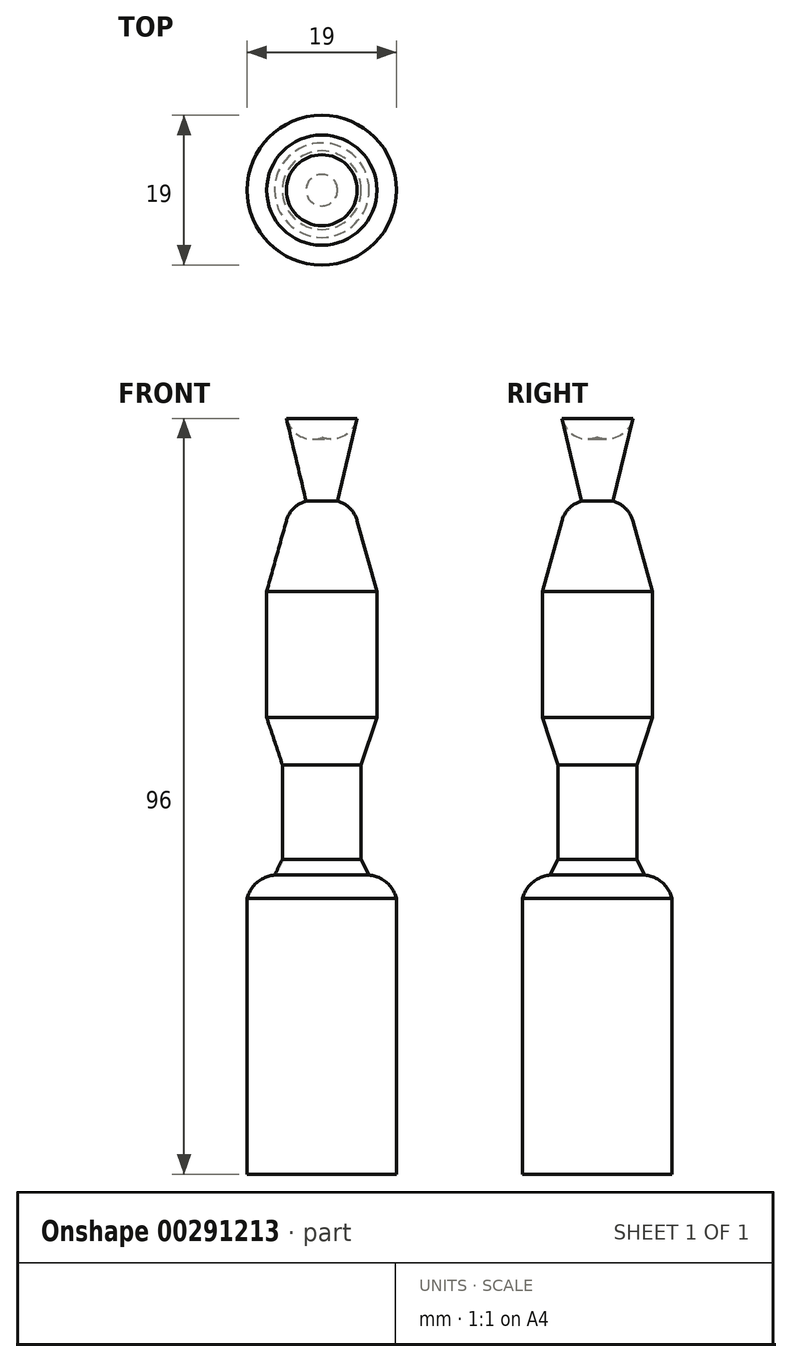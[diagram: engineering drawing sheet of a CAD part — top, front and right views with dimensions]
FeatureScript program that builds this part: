
annotation { "Feature Type Name" : "Feature", "Feature Type Description" : "" }
export const myFeature = defineFeature(function(context is Context, id is Id, definition is map)
    precondition{}
    {
        {
            var Q0;
            Q0=qCreatedBy(makeId("Front.planeOp"),FACE);
            var sketch = newSketch(context, id + "F0", { "sketchPlane" : qUnion([Q0])});
            skLineSegment(sketch, "E0", {"start": v(4.5, -4) * mm, "end": v(2, -14.5) * mm});
            skArc(sketch, "E1", {"start": v(4.5, -17) * mm, "mid": v(3.58, -15.42) * mm, "end": v(2, -14.5) * mm});
            skLineSegment(sketch, "E2", {"start": v(4.5, -17) * mm, "end": v(7, -26) * mm});
            skLineSegment(sketch, "E3", {"start": v(7, -26) * mm, "end": v(7, -42) * mm});
            skLineSegment(sketch, "E4", {"start": v(7, -42) * mm, "end": v(5, -48) * mm});
            skLineSegment(sketch, "E5", {"start": v(5, -48) * mm, "end": v(5, -60) * mm});
            skArc(sketch, "E6", {"start": v(9.5, -65) * mm, "mid": v(8.23, -62.95) * mm, "end": v(6, -62) * mm});
            skLineSegment(sketch, "E7", {"start": v(9.5, -65) * mm, "end": v(9.5, -100) * mm});
            skLineSegment(sketch, "E8", {"start": v(9.5, -100) * mm, "end": v(0, -100) * mm});
            skLineSegment(sketch, "E9", {"start": v(0, -100) * mm, "end": v(0, 0) * mm});
            skLineSegment(sketch, "E10", {"start": v(6, -62) * mm, "end": v(5, -60) * mm});
            skArc(sketch, "E11", {"start": v(4.5, -4) * mm, "mid": v(3.45, -0.65) * mm, "end": v(0, 0) * mm});
            skSolve(sketch);
        }
        {
            var Q0;
            Q0=makeQuery(id+"F0.imprint","IMPRINT",FACE,{"disambiguationData":[TD([[makeQuery(id+"F0.imprint","IMPRINT",EDGE,{"derivedFrom":sQuery(id+"F0.wireOp",EDGE,"E0")}),-1.0]])]});
            var Q1;
            Q1=sQuery(id+"F0.wireOp",EDGE,"E9");
            revolve(context, id + "F1", {"entities" : qUnion([Q0]), "axis" : qUnion([Q1]), "revolveType" : RevolveType.FULL});
        }
    });
